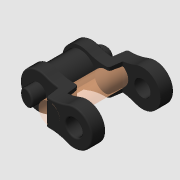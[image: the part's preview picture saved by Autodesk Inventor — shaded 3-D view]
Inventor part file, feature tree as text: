
AUTODESK INVENTOR PART (.ipt)
format: ipt  version: 2021 (Build 250183000, 183)  size: 503,296 bytes
history: native  units: in
note: dims shown in document units (in); Inventor stores cm internally (conversion verified against a paired STEP export)
features: other x4, sketch x3, extrude x3, imported_body x1
ambient origin geometry x8: Origin, YZ Plane, XZ Plane, XY Plane, X Axis, Y Axis, Z Axis, Center Point
bodies: Body1 (feature_tree), Body2 (feature_tree), Body3 (feature_tree), Body4 (feature_tree)
feature tree (11):
  parser-record x1  (decoder bookkeeping rows leaked as tree rows — omitted from the tree; the rows remain in map.json)
  imported_body  "Base1"
  sketch  "Sketch1"  dims[d0=0.046in d1=0.041in d2=0.0in]
  other  "Srf1"
  sketch  "Sketch2"  dims[d3=0.0in d4=0.046in]
  other  "Srf2"
  sketch  "Sketch3"  dims[d5=0.041in d6=0.0in d7=0.0in d8=0.0in d9=0.0in d10=0.0in d11=0.0625in d12=1.0in d13=0.0in]
  other  "Srf3"
  extrude  "ExtrusionSrf1"  Depth=0.041in TaperAngle=0.0deg
  extrude  "ExtrusionSrf2"  Depth=0.046in
  extrude  "ExtrusionSrf3"  TaperAngle=0.0deg  [1 undecoded]
note: 1 required parameter value undecoded (feature->parameter linkage not recoverable at this tier; creation-order binding heuristic only, values carry confidence <= 0.55)
